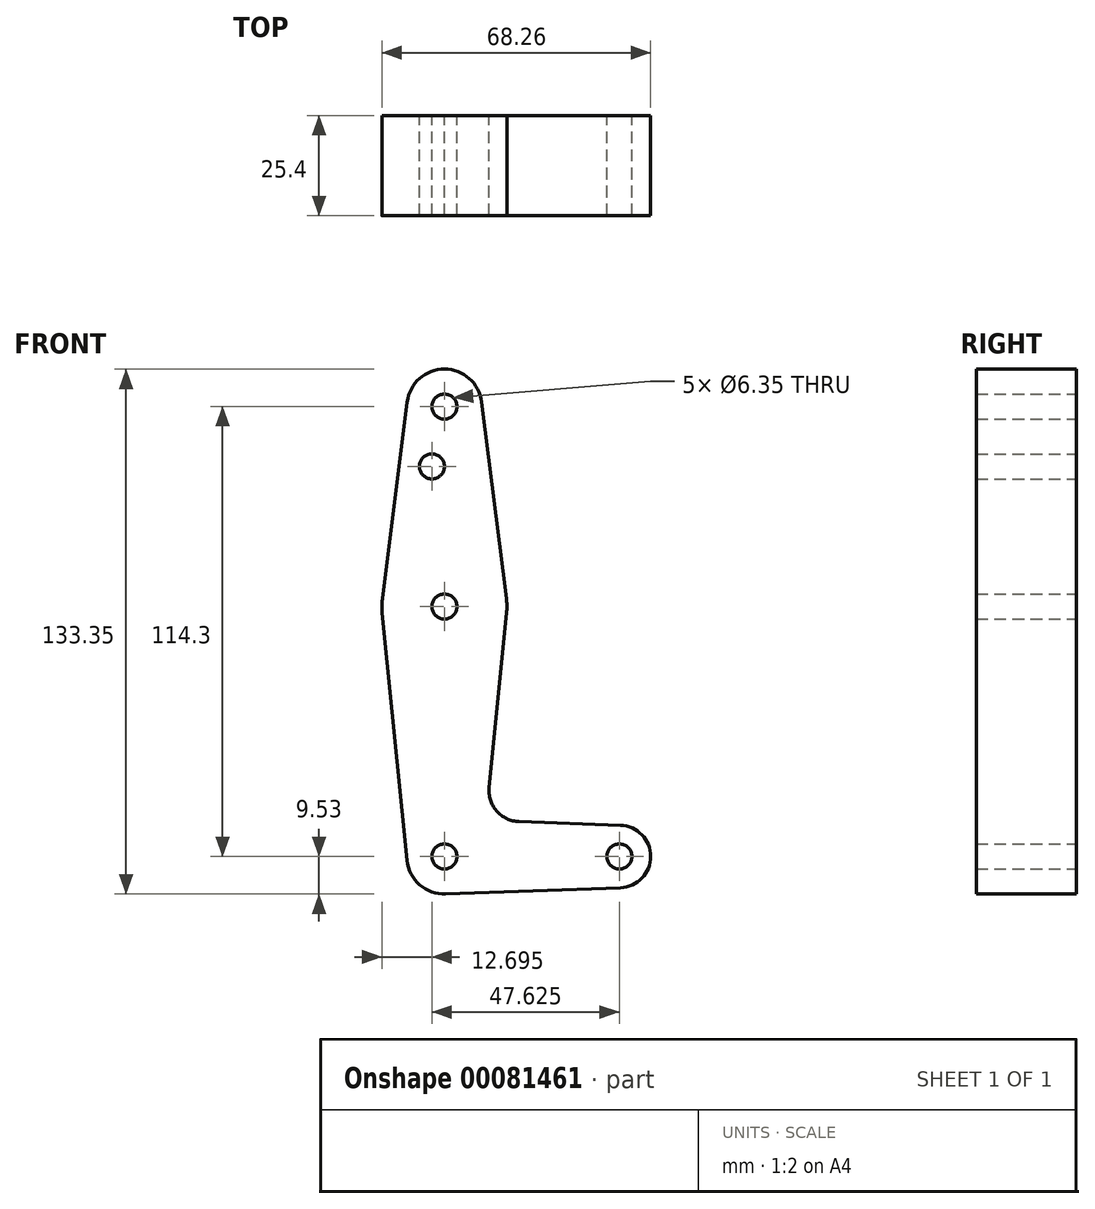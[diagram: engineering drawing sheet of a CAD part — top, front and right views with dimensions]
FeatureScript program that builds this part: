
annotation { "Feature Type Name" : "Feature", "Feature Type Description" : "" }
export const myFeature = defineFeature(function(context is Context, id is Id, definition is map)
    precondition{}
    {
        {
            var Q0;
            Q0=qCreatedBy(makeId("Front.planeOp"),FACE);
            var sketch = newSketch(context, id + "F0", { "sketchPlane" : qUnion([Q0])});
            skLineSegment(sketch, "E0", {"start": v(0, 50.8) * mm, "end": v(0, -63.5) * mm, "construction": true});
            skCircle(sketch, "E1", {"center": v(0, 50.8) * mm, "radius": 9.53 * mm});
            skCircle(sketch, "E2", {"center": v(0, 0) * mm, "radius": 15.88 * mm});
            skLineSegment(sketch, "E3", {"start": v(0, -63.5) * mm, "end": v(44.45, -63.5) * mm, "construction": true});
            skCircle(sketch, "E4", {"center": v(0, -63.5) * mm, "radius": 9.53 * mm});
            skCircle(sketch, "E5", {"center": v(44.45, -63.5) * mm, "radius": 7.94 * mm});
            skLineSegment(sketch, "E6", {"start": v(-9.45, 52) * mm, "end": v(-15.75, 1.98) * mm});
            skLineSegment(sketch, "E7", {"start": v(9.45, 52) * mm, "end": v(15.75, 1.98) * mm});
            skLineSegment(sketch, "E8", {"start": v(15.8, -1.59) * mm, "end": v(11.34, -45.9) * mm});
            skLineSegment(sketch, "E9", {"start": v(-15.8, -1.59) * mm, "end": v(-9.48, -64.45) * mm});
            skLineSegment(sketch, "E10", {"start": v(0.34, -73.02) * mm, "end": v(44.73, -71.43) * mm});
            skLineSegment(sketch, "E11", {"start": v(18.97, -54.65) * mm, "end": v(44.73, -55.57) * mm});
            skCircle(sketch, "E12", {"center": v(0, 50.8) * mm, "radius": 3.18 * mm});
            skCircle(sketch, "E13", {"center": v(0, 0) * mm, "radius": 3.18 * mm});
            skCircle(sketch, "E14", {"center": v(0, -63.5) * mm, "radius": 3.18 * mm});
            skCircle(sketch, "E15", {"center": v(44.45, -63.5) * mm, "radius": 3.18 * mm});
            skArc(sketch, "E16.filletArc", {"start": v(11.34, -45.9) * mm, "mid": v(13.26, -51.93) * mm, "end": v(18.97, -54.65) * mm});
            skCircle(sketch, "E17", {"center": v(-3.18, 35.6) * mm, "radius": 3.18 * mm});
            skSolve(sketch);
        }
        {
            var Q0;
            Q0=makeQuery(id+"F0.imprint","IMPRINT",FACE,{"disambiguationData":[TD([[makeQuery(id+"F0.imprint","IMPRINT",EDGE,{"derivedFrom":sQuery(id+"F0.wireOp",EDGE,"E12")}),-1.0]])]});
            var Q1;
            Q1=makeQuery(id+"F0.imprint","IMPRINT",FACE,{"disambiguationData":[TD([[makeQuery(id+"F0.imprint","IMPRINT",EDGE,{"derivedFrom":sQuery(id+"F0.wireOp",EDGE,"E14")}),-1.0]])]});
            var Q2;
            Q2=makeQuery(id+"F0.imprint","IMPRINT",FACE,{"disambiguationData":[TD([[makeQuery(id+"F0.imprint","IMPRINT",EDGE,{"derivedFrom":sQuery(id+"F0.wireOp",EDGE,"E15")}),-1.0]])]});
            var Q3;
            {var subQ1=sQuery(id+"F0.wireOp",EDGE,"E6");Q3=makeQuery(id+"F0.imprint","IMPRINT",FACE,{"disambiguationData":[TD([[makeQuery(id+"F0.imprint","IMPRINT",EDGE,{"derivedFrom":subQ1}),1.0]])]});}
            var Q4;
            Q4=makeQuery(id+"F0.imprint","IMPRINT",FACE,{"disambiguationData":[TD([[makeQuery(id+"F0.imprint","IMPRINT",EDGE,{"derivedFrom":sQuery(id+"F0.wireOp",EDGE,"E13")}),-1.0]])]});
            var Q5;
            {var subQ0=sQuery(id+"F0.wireOp",EDGE,"E8");Q5=makeQuery(id+"F0.imprint","IMPRINT",FACE,{"disambiguationData":[TD([[makeQuery(id+"F0.imprint","IMPRINT",EDGE,{"derivedFrom":subQ0}),-1.0]])]});}
            extrude(context, id + "F1", {"entities" : qUnion([Q0, Q1, Q2, Q3, Q4, Q5]), "depth" : 3.05 * mm});
        }
        {
            var Q0;
            Q0 = qSketchRegion(id + "F0", true);
            extrude(context, id + "F2", {"entities" : qUnion([Q0]), "operationType" : NewBodyOperationType.ADD, "depth" : 25.4 * mm});
        }
    });
